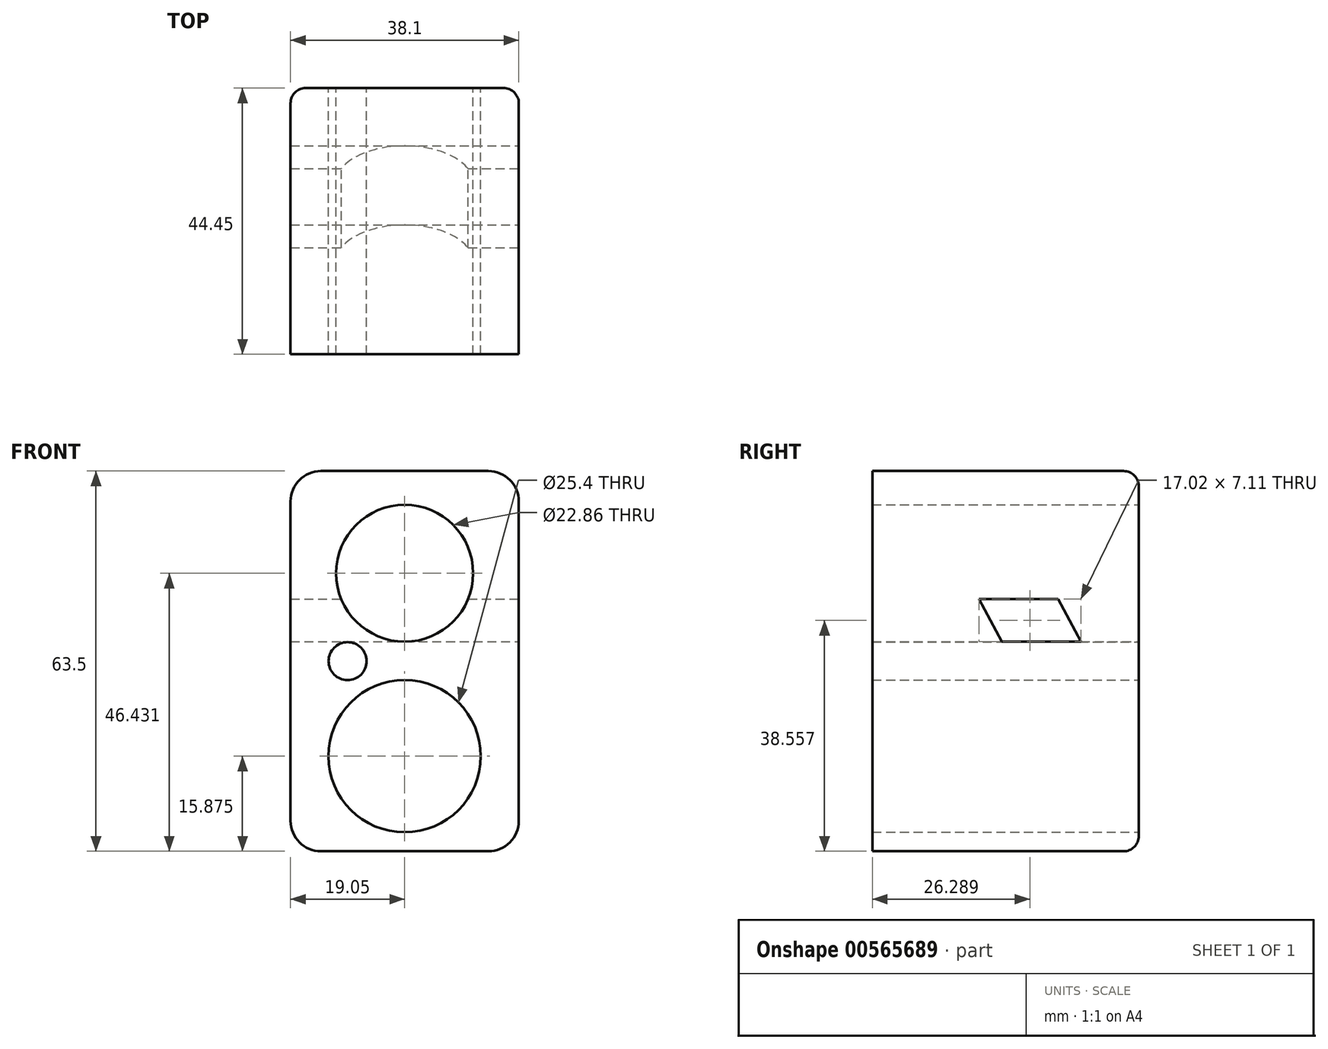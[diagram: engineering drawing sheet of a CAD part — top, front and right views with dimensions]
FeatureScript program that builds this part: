
annotation { "Feature Type Name" : "Feature", "Feature Type Description" : "" }
export const myFeature = defineFeature(function(context is Context, id is Id, definition is map)
    precondition{}
    {
        {
            var Q0;
            Q0=qCreatedBy(makeId("Front.planeOp"),FACE);
            var sketch = newSketch(context, id + "F0", { "sketchPlane" : qUnion([Q0])});
            skLineSegment(sketch, "E0.bottom", {"start": v(19.05, 31.75) * mm, "end": v(-19.05, 31.75) * mm});
            skLineSegment(sketch, "E0.top", {"start": v(19.05, -31.75) * mm, "end": v(-19.05, -31.75) * mm});
            skLineSegment(sketch, "E0.left", {"start": v(19.05, 31.75) * mm, "end": v(19.05, -31.75) * mm});
            skLineSegment(sketch, "E0.right", {"start": v(-19.05, 31.75) * mm, "end": v(-19.05, -31.75) * mm});
            skPoint(sketch, "E0.middle", {"position": v(0, 0) * mm});
            skLineSegment(sketch, "E1", {"start": v(0, 0) * mm, "end": v(-19.05, 0) * mm});
            skLineSegment(sketch, "E2", {"start": v(-19.05, 0) * mm, "end": v(-9.52, 0) * mm});
            skCircle(sketch, "E3", {"center": v(-9.52, 0) * mm, "radius": 3.18 * mm});
            skSolve(sketch);
        }
        {
            var Q0;
            Q0 = qSketchRegion(id + "F0", true);
            extrude(context, id + "F1", {"entities" : qUnion([Q0]), "depth" : 44.45 * mm, "offsetDistance" : 25.4 * mm});
        }
        {
            var Q0;
            Q0=makeQuery(id+"F1.opExtrude","CAP_FACE",FACE,{"disambiguationData":[OSD([sQuery(id+"F0.wireOp",EDGE,"E0.bottom"),sQuery(id+"F0.wireOp",EDGE,"E0.top"),sQuery(id+"F0.wireOp",EDGE,"E0.left"),sQuery(id+"F0.wireOp",EDGE,"E0.right")])],"isStart":true});
            var sketch = newSketch(context, id + "F2", { "sketchPlane" : qUnion([Q0])});
            skLineSegment(sketch, "E4", {"start": v(0, -31.75) * mm, "end": v(0, -28.57) * mm});
            skLineSegment(sketch, "E5", {"start": v(0, -28.57) * mm, "end": v(0, -15.87) * mm});
            skCircle(sketch, "E6", {"center": v(0, -15.87) * mm, "radius": 12.7 * mm});
            skLineSegment(sketch, "E7", {"start": v(0, -15.87) * mm, "end": v(0, -3.17) * mm});
            skLineSegment(sketch, "E8", {"start": v(0, -3.17) * mm, "end": v(0, 5.8) * mm});
            skLineSegment(sketch, "E9", {"start": v(0, 5.8) * mm, "end": v(0, 14.68) * mm});
            skCircle(sketch, "E10", {"center": v(0, 14.68) * mm, "radius": 11.43 * mm});
            skLineSegment(sketch, "E11", {"start": v(0, 3.25) * mm, "end": v(-19.05, 3.25) * mm});
            skLineSegment(sketch, "E12", {"start": v(0, -15.87) * mm, "end": v(19.05, -15.87) * mm});
            skLineSegment(sketch, "E13", {"start": v(19.05, -15.87) * mm, "end": v(-19.05, -15.87) * mm});
            skSolve(sketch);
        }
        {
            var Q0;
            Q0 = qSketchRegion(id + "F2", true);
            extrude(context, id + "F3", {"entities" : qUnion([Q0]), "operationType" : NewBodyOperationType.REMOVE, "endBound" : BoundingType.THROUGH_ALL, "oppositeDirection" : true, "depth" : 25.4 * mm, "offsetDistance" : 25.4 * mm});
        }
        {
            var Q0;
            Q0=makeQuery(id+"F1.opExtrude","SWEPT_FACE",FACE,{"disambiguationData":[OSD([sQuery(id+"F0.wireOp",EDGE,"E0.left")])]});
            var sketch = newSketch(context, id + "F4", { "sketchPlane" : qUnion([Q0])});
            skLineSegment(sketch, "E14", {"start": v(0, 0) * mm, "end": v(0, 3.25) * mm});
            skLineSegment(sketch, "E15", {"start": v(0, 3.25) * mm, "end": v(-44.45, 3.25) * mm});
            skLineSegment(sketch, "E16", {"start": v(-44.45, 3.25) * mm, "end": v(-26.67, 3.25) * mm});
            skLineSegment(sketch, "E17", {"start": v(-26.67, 3.25) * mm, "end": v(-26.67, 10.36) * mm});
            skLineSegment(sketch, "E18", {"start": v(-44.45, 3.25) * mm, "end": v(-22.86, 3.25) * mm});
            skLineSegment(sketch, "E19", {"start": v(-22.86, 3.25) * mm, "end": v(-26.67, 10.36) * mm});
            skLineSegment(sketch, "E20", {"start": v(-22.86, 3.25) * mm, "end": v(-9.65, 3.25) * mm});
            skLineSegment(sketch, "E21", {"start": v(-9.65, 3.25) * mm, "end": v(-13.46, 10.36) * mm});
            skLineSegment(sketch, "E22", {"start": v(-13.46, 10.36) * mm, "end": v(-26.67, 10.36) * mm});
            skSolve(sketch);
        }
        {
            var Q0;
            Q0=makeQuery(id+"F4.imprint","IMPRINT",FACE,{"disambiguationData":[TD([[makeQuery(id+"F4.imprint","IMPRINT",EDGE,{"derivedFrom":sQuery(id+"F4.wireOp",EDGE,"E19")}),-1.0]])]});
            extrude(context, id + "F5", {"entities" : qUnion([Q0]), "operationType" : NewBodyOperationType.REMOVE, "endBound" : BoundingType.THROUGH_ALL, "oppositeDirection" : true, "depth" : 25.4 * mm, "offsetDistance" : 25.4 * mm});
        }
        {
            var Q0;
            Q0=makeQuery(id+"F1.opExtrude","SWEPT_EDGE",EDGE,{"disambiguationData":[OSD([sQuery(id+"F0.wireOp",EDGE,"E0.bottom"),sQuery(id+"F0.wireOp",EDGE,"E0.right")])]});
            var Q1;
            Q1=makeQuery(id+"F1.opExtrude","SWEPT_EDGE",EDGE,{"disambiguationData":[OSD([sQuery(id+"F0.wireOp",EDGE,"E0.bottom"),sQuery(id+"F0.wireOp",EDGE,"E0.left")])]});
            fillet(context, id + "F6", {"entities" : qUnion([Q0, Q1]), "radius" : 5.08 * mm, "tangentPropagation" : true, "allowEdgeOverflow" : false});
        }
        {
            var Q0;
            Q0=makeQuery(id+"F1.opExtrude","SWEPT_EDGE",EDGE,{"disambiguationData":[OSD([sQuery(id+"F0.wireOp",EDGE,"E0.top"),sQuery(id+"F0.wireOp",EDGE,"E0.left")])]});
            var Q1;
            Q1=makeQuery(id+"F1.opExtrude","SWEPT_EDGE",EDGE,{"disambiguationData":[OSD([sQuery(id+"F0.wireOp",EDGE,"E0.top"),sQuery(id+"F0.wireOp",EDGE,"E0.right")])]});
            fillet(context, id + "F7", {"entities" : qUnion([Q0, Q1]), "radius" : 5.08 * mm, "tangentPropagation" : true, "allowEdgeOverflow" : false});
        }
        {
            var Q0;
            Q0=makeQuery(id+"F1.opExtrude","CAP_EDGE",EDGE,{"disambiguationData":[OSD([sQuery(id+"F0.wireOp",EDGE,"E0.bottom")])],"isStart":true});
            fillet(context, id + "F8", {"entities" : qUnion([Q0]), "radius" : 2.54 * mm, "tangentPropagation" : true, "allowEdgeOverflow" : false});
        }
    });
